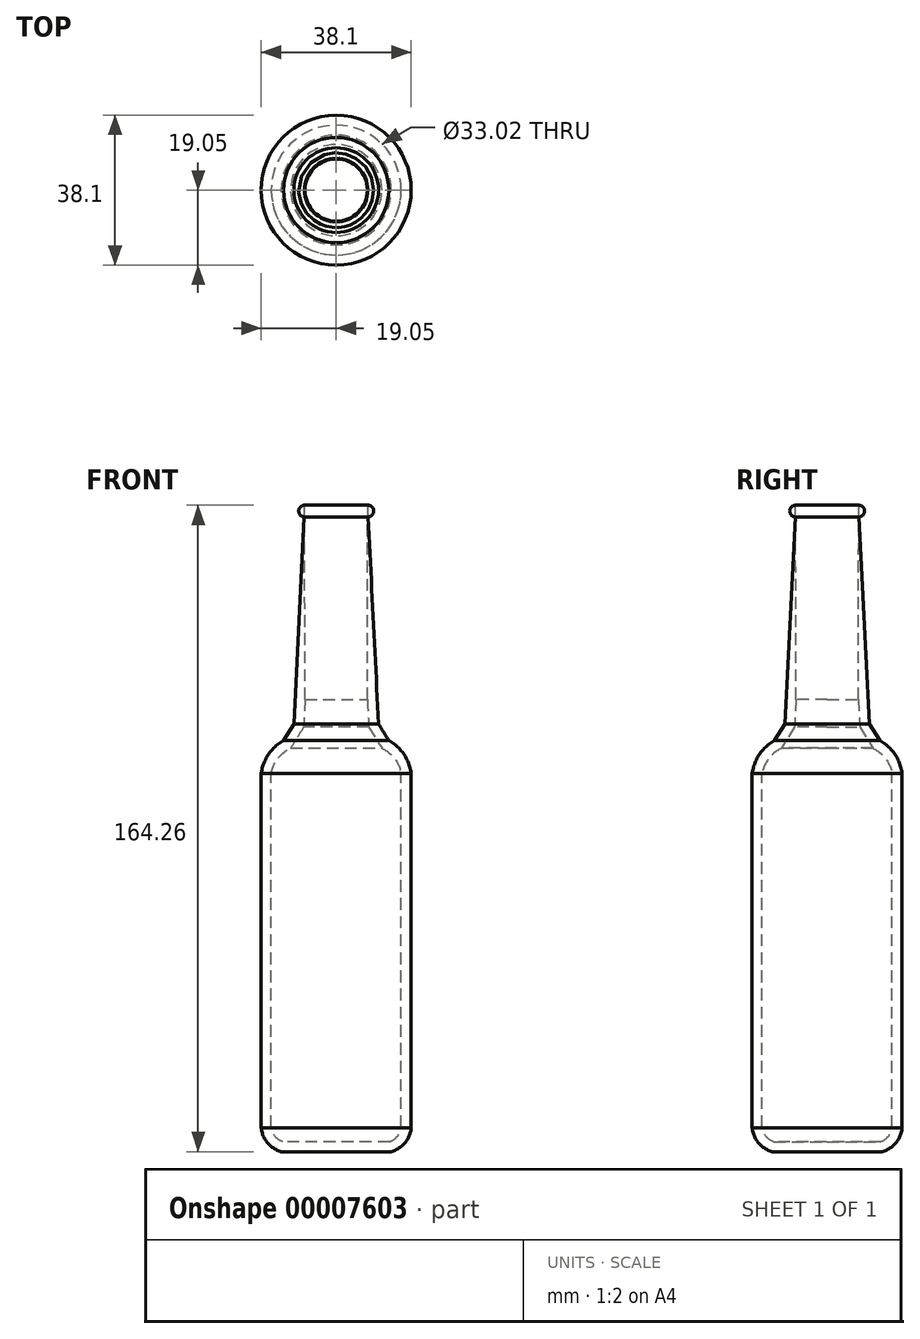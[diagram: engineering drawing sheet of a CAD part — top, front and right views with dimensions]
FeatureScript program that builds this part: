
annotation { "Feature Type Name" : "Feature", "Feature Type Description" : "" }
export const myFeature = defineFeature(function(context is Context, id is Id, definition is map)
    precondition{}
    {
        {
            var Q0;
            Q0=qCreatedBy(makeId("Front.planeOp"),FACE);
            var sketch = newSketch(context, id + "F0", { "sketchPlane" : qUnion([Q0])});
            skLineSegment(sketch, "E0", {"start": v(0, 59.34) * mm, "end": v(0, -105.76) * mm});
            skLineSegment(sketch, "E1", {"start": v(0, -80.66) * mm, "end": v(-19.05, -80.66) * mm, "construction": true});
            skLineSegment(sketch, "E2", {"start": v(0, -105.76) * mm, "end": v(-13.97, -105.76) * mm});
            skLineSegment(sketch, "E3", {"start": v(-19.05, -103.65) * mm, "end": v(-19.05, -9.67) * mm});
            skLineSegment(sketch, "E4", {"start": v(-19.05, -9.67) * mm, "end": v(0, -9.67) * mm});
            skLineSegment(sketch, "E5", {"start": v(-9.52, -9.67) * mm, "end": v(-9.53, 72.3) * mm, "construction": true});
            skLineSegment(sketch, "E6", {"start": v(8.17, -105.76) * mm, "end": v(8.17, -0.98) * mm, "construction": true});
            skArc(sketch, "E7", {"start": v(-9.52, 0) * mm, "mid": v(-15.9, -3.24) * mm, "end": v(-19.05, -9.67) * mm});
            skArc(sketch, "E8", {"start": v(-19.05, -98.5) * mm, "mid": v(-17.82, -103.05) * mm, "end": v(-13.97, -105.76) * mm});
            skLineSegment(sketch, "E9", {"start": v(-10.92, -0.3) * mm, "end": v(-8.03, 57.01) * mm});
            skLineSegment(sketch, "E10", {"start": v(-8.03, 57.01) * mm, "end": v(0, 57.01) * mm});
            skCircle(sketch, "E11", {"center": v(-8.03, 57.01) * mm, "radius": 1.5 * mm});
            skLineSegment(sketch, "E12", {"start": v(-8.04, 58.5) * mm, "end": v(0, 58.52) * mm});
            skSolve(sketch);
        }
        {
            var Q0;
            {var subQ8=sQuery(id+"F0.wireOp",EDGE,"E4");Q0=makeQuery(id+"F0.imprint","IMPRINT",FACE,{"disambiguationData":[TD([[makeQuery(id+"F0.imprint","IMPRINT",EDGE,{"derivedFrom":subQ8}),1.0]])]});}
            var Q1;
            {var subQ1=sQuery(id+"F0.wireOp",EDGE,"E2");Q1=makeQuery(id+"F0.imprint","IMPRINT",FACE,{"disambiguationData":[TD([[makeQuery(id+"F0.imprint","IMPRINT",EDGE,{"derivedFrom":subQ1}),-1.0]])]});}
            var Q2;
            {var subQ1=sQuery(id+"F0.wireOp",EDGE,"894c5b9f-35cf-4cfa-8ba2-697312b85305");var subQ5=sQuery(id+"F0.wireOp",EDGE,"b8ee942f-dd23-47e8-8127-fa3aafc0242a");var subQ6=makeQuery(id+"F0.imprint","INTERSECT",VERTEX,{"derivedFrom":[subQ5,subQ1]});Q2=makeQuery(id+"F0.imprint","IMPRINT",FACE,{"disambiguationData":[TD([[makeQuery(id+"F0.imprint","IMPRINT",EDGE,{"disambiguationData":[TD([[subQ6,1.0]])],"derivedFrom":subQ1}),-1.0]])]});}
            var Q3;
            {var subQ2=sQuery(id+"F0.wireOp",EDGE,"044f2e1a-76f1-4475-8fa2-807f1b795be7");var subQ4=sQuery(id+"F0.wireOp",EDGE,"b8ee942f-dd23-47e8-8127-fa3aafc0242a");var subQ6=makeQuery(id+"F0.imprint","INTERSECT",VERTEX,{"derivedFrom":[subQ2,subQ4]});Q3=makeQuery(id+"F0.imprint","IMPRINT",FACE,{"disambiguationData":[TD([[makeQuery(id+"F0.imprint","IMPRINT",EDGE,{"disambiguationData":[TD([[subQ6,-1.0]])],"derivedFrom":subQ4}),1.0]])]});}
            var Q4;
            {var subQ0=sQuery(id+"F0.wireOp",EDGE,"850e35e8-23a5-42b4-a5c1-ddac0515076f");var subQ1=sQuery(id+"F0.wireOp",EDGE,"894c5b9f-35cf-4cfa-8ba2-697312b85305");var subQ2=makeQuery(id+"F0.imprint","INTERSECT",VERTEX,{"derivedFrom":[subQ1,subQ0]});Q4=makeQuery(id+"F0.imprint","IMPRINT",FACE,{"disambiguationData":[TD([[makeQuery(id+"F0.imprint","IMPRINT",EDGE,{"disambiguationData":[TD([[subQ2,1.0]])],"derivedFrom":subQ1}),1.0]])]});}
            var Q5;
            {var subQ3=sQuery(id+"F0.wireOp",EDGE,"044f2e1a-76f1-4475-8fa2-807f1b795be7");var subQ5=sQuery(id+"F0.wireOp",EDGE,"b8ee942f-dd23-47e8-8127-fa3aafc0242a");var subQ7=makeQuery(id+"F0.imprint","INTERSECT",VERTEX,{"derivedFrom":[subQ3,subQ5]});Q5=makeQuery(id+"F0.imprint","IMPRINT",FACE,{"disambiguationData":[TD([[makeQuery(id+"F0.imprint","IMPRINT",EDGE,{"disambiguationData":[TD([[subQ7,-1.0]])],"derivedFrom":subQ5}),-1.0]])]});}
            var Q6;
            {var subQ4=sQuery(id+"F0.wireOp",EDGE,"18bd5946-7567-4094-a345-ae22318f4017");Q6=makeQuery(id+"F0.imprint","IMPRINT",FACE,{"disambiguationData":[TD([[makeQuery(id+"F0.imprint","IMPRINT",EDGE,{"derivedFrom":subQ4}),-1.0]])]});}
            var Q7;
            {var subQ1=sQuery(id+"F0.wireOp",EDGE,"762228d0-d386-4ad8-a3bf-4fd26f2c354e");var subQ3=sQuery(id+"F0.wireOp",EDGE,"318b3eee-1ee5-4fc5-9fdd-7debef153779");var subQ5=makeQuery(id+"F0.imprint","INTERSECT",VERTEX,{"derivedFrom":[subQ3,subQ1]});Q7=makeQuery(id+"F0.imprint","IMPRINT",FACE,{"disambiguationData":[TD([[makeQuery(id+"F0.imprint","IMPRINT",EDGE,{"disambiguationData":[TD([[subQ5,1.0]])],"derivedFrom":subQ3}),-1.0]])]});}
            var Q8;
            {var subQ1=sQuery(id+"F0.wireOp",EDGE,"318b3eee-1ee5-4fc5-9fdd-7debef153779");var subQ4=sQuery(id+"F0.wireOp",EDGE,"762228d0-d386-4ad8-a3bf-4fd26f2c354e");var subQ6=makeQuery(id+"F0.imprint","INTERSECT",VERTEX,{"derivedFrom":[subQ1,subQ4]});Q8=makeQuery(id+"F0.imprint","IMPRINT",FACE,{"disambiguationData":[TD([[makeQuery(id+"F0.imprint","IMPRINT",EDGE,{"disambiguationData":[TD([[subQ6,1.0]])],"derivedFrom":subQ1}),1.0]])]});}
            var Q9;
            {var subQ1=sQuery(id+"F0.wireOp",EDGE,"8c721777-8091-493b-b208-a316498cd9de");Q9=makeQuery(id+"F0.imprint","IMPRINT",FACE,{"disambiguationData":[TD([[makeQuery(id+"F0.imprint","IMPRINT",EDGE,{"derivedFrom":subQ1}),-1.0]])]});}
            var Q10;
            {var subQ1=sQuery(id+"F0.wireOp",EDGE,"ea3d5a01-0667-447d-8058-f9cf13f932bc");var subQ3=sQuery(id+"F0.wireOp",EDGE,"45986dd5-7632-43ce-8b9b-b260021bbbcb");var subQ5=makeQuery(id+"F0.imprint","INTERSECT",VERTEX,{"derivedFrom":[subQ3,subQ1]});Q10=makeQuery(id+"F0.imprint","IMPRINT",FACE,{"disambiguationData":[TD([[makeQuery(id+"F0.imprint","IMPRINT",EDGE,{"disambiguationData":[TD([[subQ5,1.0]])],"derivedFrom":subQ3}),-1.0]])]});}
            var Q11;
            {var subQ1=sQuery(id+"F0.wireOp",EDGE,"bdc092f0-3e34-4d5e-9ac3-1e113eabc6b1");Q11=makeQuery(id+"F0.imprint","IMPRINT",FACE,{"disambiguationData":[TD([[makeQuery(id+"F0.imprint","IMPRINT",EDGE,{"derivedFrom":subQ1}),-1.0]])]});}
            var Q12;
            {var subQ1=sQuery(id+"F0.wireOp",EDGE,"45986dd5-7632-43ce-8b9b-b260021bbbcb");var subQ4=sQuery(id+"F0.wireOp",EDGE,"ea3d5a01-0667-447d-8058-f9cf13f932bc");var subQ6=makeQuery(id+"F0.imprint","INTERSECT",VERTEX,{"derivedFrom":[subQ1,subQ4]});Q12=makeQuery(id+"F0.imprint","IMPRINT",FACE,{"disambiguationData":[TD([[makeQuery(id+"F0.imprint","IMPRINT",EDGE,{"disambiguationData":[TD([[subQ6,1.0]])],"derivedFrom":subQ1}),1.0]])]});}
            var Q13;
            {var subQ0=sQuery(id+"F0.wireOp",EDGE,"E12");Q13=makeQuery(id+"F0.imprint","IMPRINT",FACE,{"disambiguationData":[TD([[makeQuery(id+"F0.imprint","IMPRINT",EDGE,{"derivedFrom":subQ0}),-1.0]])]});}
            var Q14;
            {var subQ1=sQuery(id+"F0.wireOp",EDGE,"E10");var subQ3=sQuery(id+"F0.wireOp",EDGE,"E9");var subQ5=makeQuery(id+"F0.imprint","INTERSECT",VERTEX,{"derivedFrom":[subQ3,subQ1]});Q14=makeQuery(id+"F0.imprint","IMPRINT",FACE,{"disambiguationData":[TD([[makeQuery(id+"F0.imprint","IMPRINT",EDGE,{"disambiguationData":[TD([[subQ5,1.0]])],"derivedFrom":subQ3}),-1.0]])]});}
            var Q15;
            {var subQ1=sQuery(id+"F0.wireOp",EDGE,"E9");var subQ4=sQuery(id+"F0.wireOp",EDGE,"E10");var subQ6=makeQuery(id+"F0.imprint","INTERSECT",VERTEX,{"derivedFrom":[subQ1,subQ4]});Q15=makeQuery(id+"F0.imprint","IMPRINT",FACE,{"disambiguationData":[TD([[makeQuery(id+"F0.imprint","IMPRINT",EDGE,{"disambiguationData":[TD([[subQ6,1.0]])],"derivedFrom":subQ1}),1.0]])]});}
            var Q16;
            Q16=sQuery(id+"F0.wireOp",EDGE,"E0");
            revolve(context, id + "F1", {"entities" : qUnion([Q0, Q1, Q2, Q3, Q4, Q5, Q6, Q7, Q8, Q9, Q10, Q11, Q12, Q13, Q14, Q15]), "axis" : qUnion([Q16]), "revolveType" : RevolveType.FULL});
        }
        {
            var Q0;
            Q0=makeQuery(id+"F1.opRevolve","SWEPT_EDGE",EDGE,{"disambiguationData":[OSD([sQuery(id+"F0.wireOp",EDGE,"E7"),sQuery(id+"F0.wireOp",EDGE,"E9")])]});
            chamfer(context, id + "F2", {"entities" : qUnion([Q0]), "width" : 5.08 * mm, "tangentPropagation" : true});
        }
        {
            var Q0;
            Q0=makeQuery(id+"F1.opRevolve","SWEPT_FACE",FACE,{"disambiguationData":[OSD([sQuery(id+"F0.wireOp",EDGE,"E12")])]});
            shell(context, id + "F3", {"entities" : qUnion([Q0]), "thickness" : 2.54 * mm});
        }
    });
